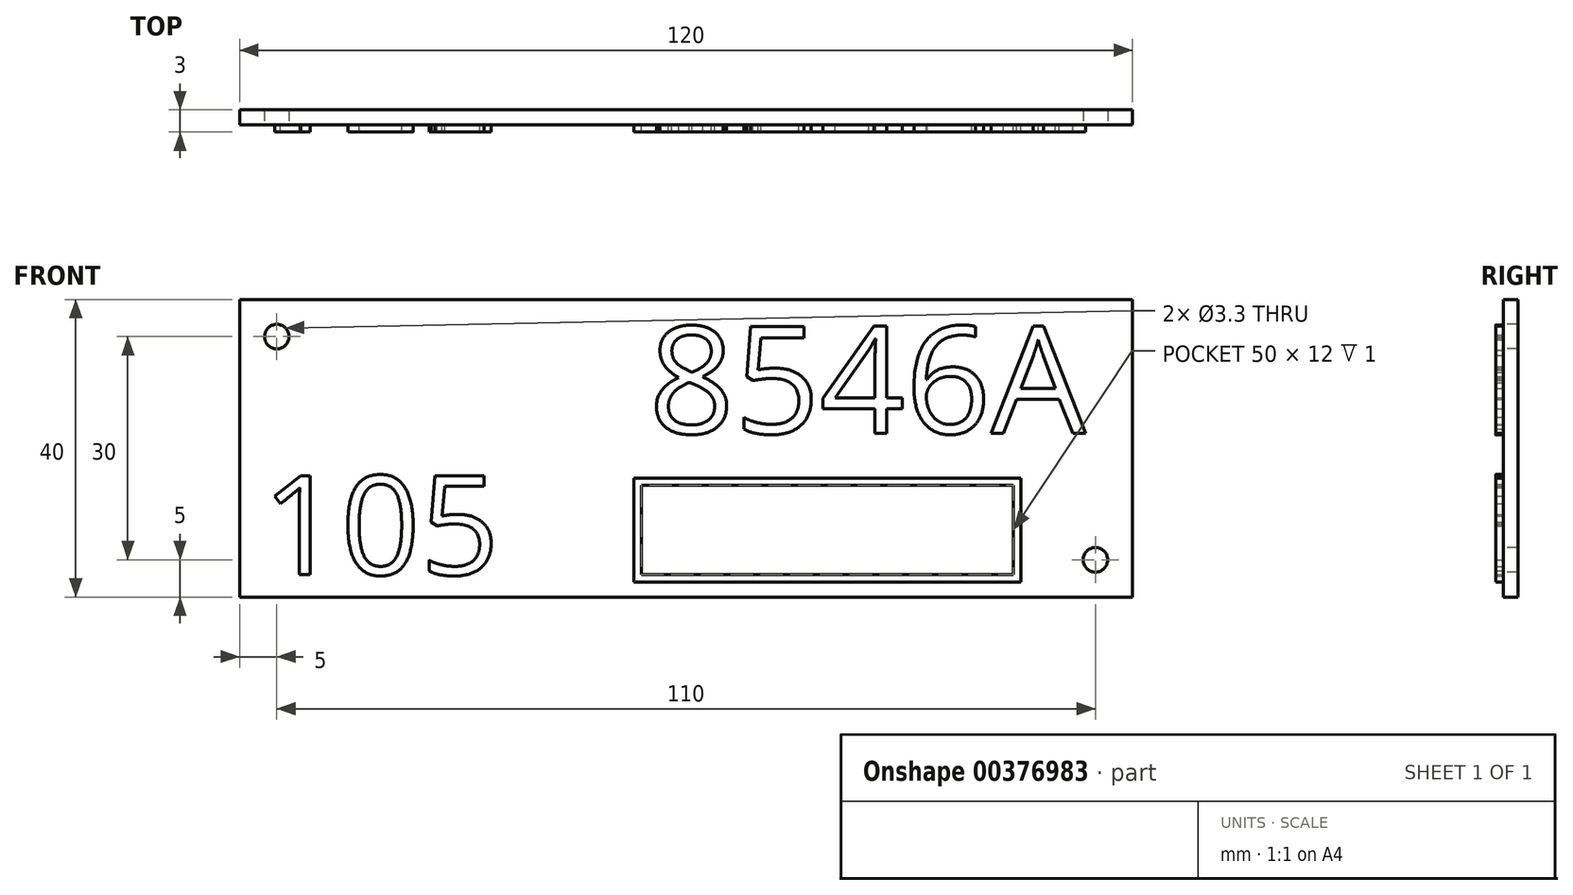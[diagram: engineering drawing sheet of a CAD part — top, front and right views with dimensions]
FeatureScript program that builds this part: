
annotation { "Feature Type Name" : "Feature", "Feature Type Description" : "" }
export const myFeature = defineFeature(function(context is Context, id is Id, definition is map)
    precondition{}
    {
        {
            var Q0;
            Q0=qCreatedBy(makeId("Front.planeOp"),FACE);
            var sketch = newSketch(context, id + "F0", { "sketchPlane" : qUnion([Q0])});
            skLineSegment(sketch, "E0.bottom", {"start": v(60, -20) * mm, "end": v(-60, -20) * mm});
            skLineSegment(sketch, "E0.top", {"start": v(60, 20) * mm, "end": v(-60, 20) * mm});
            skLineSegment(sketch, "E0.left", {"start": v(60, -20) * mm, "end": v(60, 20) * mm});
            skLineSegment(sketch, "E0.right", {"start": v(-60, -20) * mm, "end": v(-60, 20) * mm});
            skPoint(sketch, "E0.middle", {"position": v(0, 0) * mm});
            skSolve(sketch);
        }
        {
            var Q0;
            Q0=makeQuery(id+"F0.imprint","IMPRINT",FACE,{"disambiguationData":[TD([[makeQuery(id+"F0.imprint","IMPRINT",EDGE,{"derivedFrom":sQuery(id+"F0.wireOp",EDGE,"E0.bottom")}),-1.0]])]});
            extrude(context, id + "F1", {"entities" : qUnion([Q0]), "depth" : 2 * mm});
        }
        {
            var Q0;
            Q0=makeQuery(id+"F1.opExtrude","CAP_FACE",FACE,{"disambiguationData":[OSD([sQuery(id+"F0.wireOp",EDGE,"E0.bottom"),sQuery(id+"F0.wireOp",EDGE,"E0.top"),sQuery(id+"F0.wireOp",EDGE,"E0.left"),sQuery(id+"F0.wireOp",EDGE,"E0.right")])],"isStart":false});
            var sketch = newSketch(context, id + "F2", { "sketchPlane" : qUnion([Q0])});
            skPoint(sketch, "E1", {"position": v(-55, 15) * mm});
            skPoint(sketch, "E2", {"position": v(55, -15) * mm});
            skSolve(sketch);
        }
        {
            var Q0;
            Q0=sQuery(id+"F2.wireOp",VERTEX,"E1");
            var Q1;
            Q1=sQuery(id+"F2.wireOp",VERTEX,"E2");
            var Q2;
            Q2=makeQuery(id+"F1.opExtrude","SWEPT_BODY",BODY,{"disambiguationData":[OSD([sQuery(id+"F0.wireOp",EDGE,"E0.bottom"),sQuery(id+"F0.wireOp",EDGE,"E0.top"),sQuery(id+"F0.wireOp",EDGE,"E0.left"),sQuery(id+"F0.wireOp",EDGE,"E0.right")])]});
            hole(context, id + "F3", {"style" : HoleStyle.SIMPLE, "endStyle" : HoleEndStyle.THROUGH, "holeDiameter" : 3.3 * mm, "locations" : qUnion([Q0, Q1]), "scope" : qUnion([Q2]), "isTappedThrough" : true});
        }
        {
            var Q0;
            Q0=makeQuery(id+"F1.opExtrude","CAP_FACE",FACE,{"disambiguationData":[OSD([sQuery(id+"F0.wireOp",EDGE,"E0.bottom"),sQuery(id+"F0.wireOp",EDGE,"E0.top"),sQuery(id+"F0.wireOp",EDGE,"E0.left"),sQuery(id+"F0.wireOp",EDGE,"E0.right")])],"isStart":false});
            var sketch = newSketch(context, id + "F4", { "sketchPlane" : qUnion([Q0])});
            skText(sketch, "E3", { "text": "8546A", "fontName": "OpenSans-Regular.ttf"});
            const initialGuessF4  = {"E3": [-0.005, 0.002, 1, 0, 0.01447]};
            skSetInitialGuess(sketch, initialGuessF4);
            skSolve(sketch);
        }
        {
            var Q0;
            Q0=qSketchRegion(id+"F4",true);
            extrude(context, id + "F5", {"entities" : qUnion([Q0]), "operationType" : NewBodyOperationType.ADD, "depth" : 1 * mm});
        }
        {
            var Q0;
            {var subQ0=sQuery(id+"F0.wireOp",EDGE,"E0.top");var subQ1=sQuery(id+"F0.wireOp",EDGE,"E0.left");var subQ2=sQuery(id+"F0.wireOp",EDGE,"E0.right");var subQ3=sQuery(id+"F0.wireOp",EDGE,"E0.bottom");Q0=makeQuery(id+"F5.boolean.opBoolean","SPLIT",FACE,{"disambiguationData":[TD([makeQuery(id+"F1.opExtrude","SWEPT_FACE",FACE,{"disambiguationData":[OSD([subQ3])]})])],"derivedFrom":makeQuery(id+"F1.opExtrude","CAP_FACE",FACE,{"disambiguationData":[OSD([subQ3,subQ0,subQ1,subQ2])],"isStart":false})});}
            var sketch = newSketch(context, id + "F6", { "sketchPlane" : qUnion([Q0])});
            skText(sketch, "E4", { "text": "105", "fontName": "OpenSans-Regular.ttf"});
            const initialGuessF6  = {"E4": [-0.057, -0.017, 1, 0, 0.01338]};
            skSetInitialGuess(sketch, initialGuessF6);
            skSolve(sketch);
        }
        {
            var Q0;
            Q0=qSketchRegion(id+"F6",true);
            extrude(context, id + "F7", {"entities" : qUnion([Q0]), "operationType" : NewBodyOperationType.ADD, "depth" : 1 * mm});
        }
        {
            var Q0;
            {var subQ46=sQuery(id+"F0.wireOp",EDGE,"E0.top");var subQ48=sQuery(id+"F0.wireOp",EDGE,"E0.left");var subQ66=sQuery(id+"F0.wireOp",EDGE,"E0.right");var subQ76=sQuery(id+"F0.wireOp",EDGE,"E0.bottom");var subQ77=makeQuery(id+"F1.opExtrude","SWEPT_FACE",FACE,{"disambiguationData":[OSD([subQ76])]});Q0=makeQuery(id+"F7.boolean.opBoolean","SPLIT",FACE,{"disambiguationData":[TD([subQ77])],"derivedFrom":makeQuery(id+"F5.boolean.opBoolean","SPLIT",FACE,{"disambiguationData":[TD([subQ77])],"derivedFrom":makeQuery(id+"F1.opExtrude","CAP_FACE",FACE,{"disambiguationData":[OSD([subQ76,subQ46,subQ48,subQ66])],"isStart":false})})});}
            var sketch = newSketch(context, id + "F8", { "sketchPlane" : qUnion([Q0])});
            skLineSegment(sketch, "E5.bottom", {"start": v(45, -18) * mm, "end": v(-7, -18) * mm});
            skLineSegment(sketch, "E5.top", {"start": v(45, -4) * mm, "end": v(-7, -4) * mm});
            skLineSegment(sketch, "E5.left", {"start": v(45, -18) * mm, "end": v(45, -4) * mm});
            skLineSegment(sketch, "E5.right", {"start": v(-7, -18) * mm, "end": v(-7, -4) * mm});
            skPoint(sketch, "E5.middle", {"position": v(19, -11) * mm});
            skLineSegment(sketch, "E6.0", {"start": v(44, -5) * mm, "end": v(-6, -5) * mm});
            skLineSegment(sketch, "E6.1", {"start": v(44, -17) * mm, "end": v(44, -5) * mm});
            skLineSegment(sketch, "E6.2", {"start": v(44, -17) * mm, "end": v(-6, -17) * mm});
            skLineSegment(sketch, "E6.3", {"start": v(-6, -17) * mm, "end": v(-6, -5) * mm});
            skSolve(sketch);
        }
        {
            var Q0;
            Q0=makeQuery(id+"F8.imprint","IMPRINT",FACE,{"disambiguationData":[TD([[makeQuery(id+"F8.imprint","IMPRINT",EDGE,{"derivedFrom":sQuery(id+"F8.wireOp",EDGE,"E5.bottom")}),-1.0]])]});
            extrude(context, id + "F9", {"entities" : qUnion([Q0]), "operationType" : NewBodyOperationType.ADD, "depth" : 1 * mm});
        }
    });
